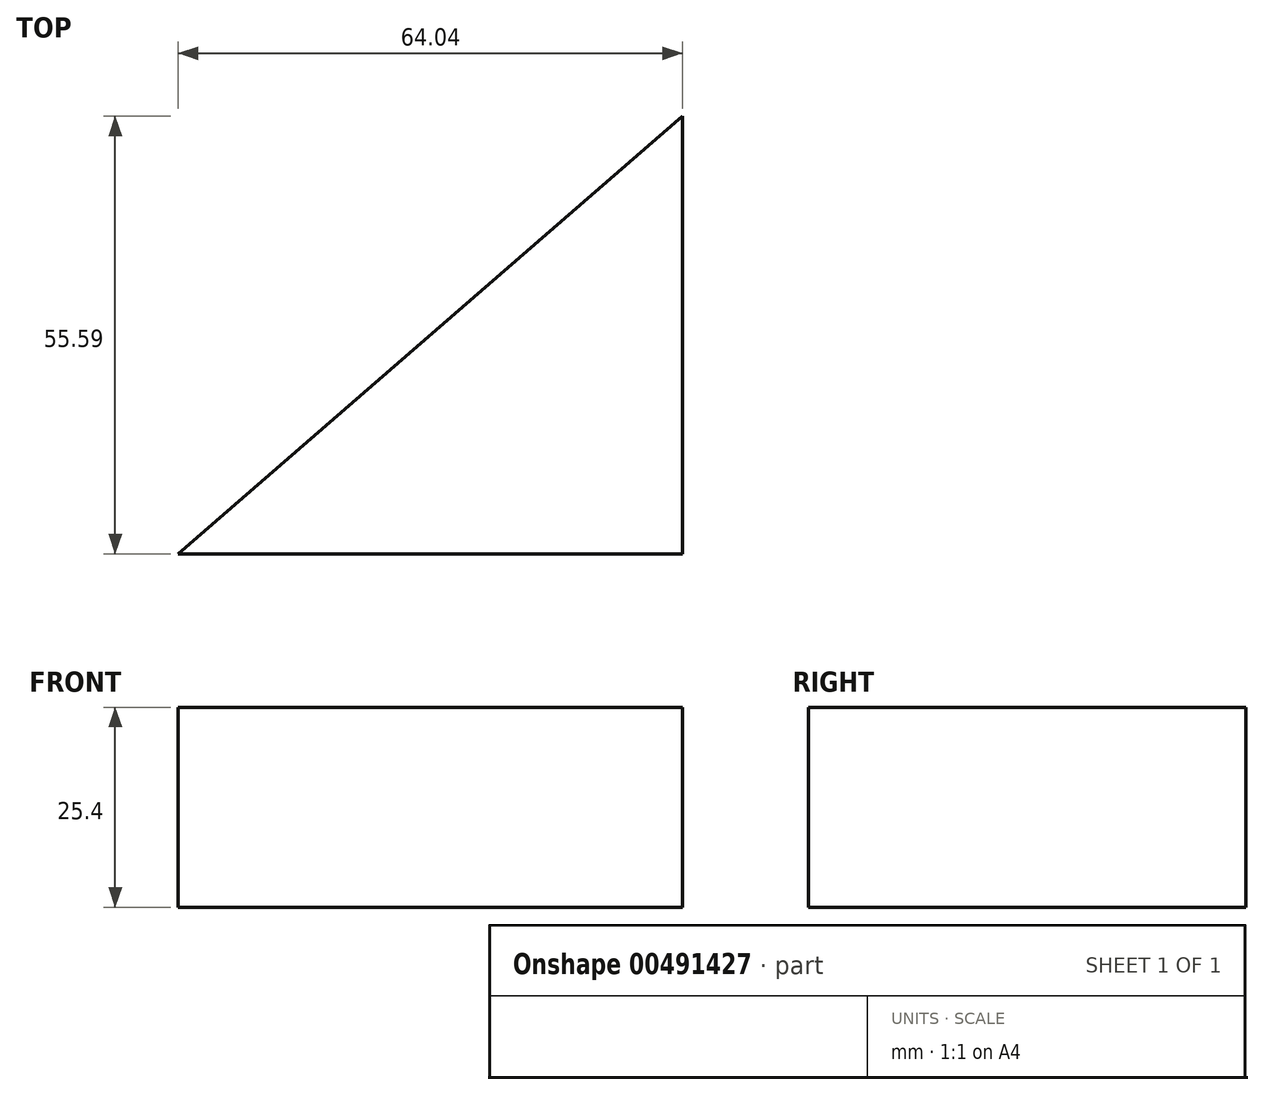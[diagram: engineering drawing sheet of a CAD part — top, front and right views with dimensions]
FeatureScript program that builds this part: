
annotation { "Feature Type Name" : "Feature", "Feature Type Description" : "" }
export const myFeature = defineFeature(function(context is Context, id is Id, definition is map)
    precondition{}
    {
        {
            var Q0;
            Q0=qCreatedBy(makeId("Top.planeOp"),FACE);
            var sketch = newSketch(context, id + "F0", { "sketchPlane" : qUnion([Q0])});
            skLineSegment(sketch, "E0", {"start": v(0, 0) * mm, "end": v(64.04, 55.6) * mm});
            skLineSegment(sketch, "E1", {"start": v(64.04, 55.6) * mm, "end": v(64.04, 0) * mm});
            skLineSegment(sketch, "E2", {"start": v(64.04, 0) * mm, "end": v(0, 0) * mm});
            skSolve(sketch);
        }
        {
            var Q0;
            Q0=makeQuery(id+"F0.imprint","IMPRINT",FACE,{"disambiguationData":[TD([[makeQuery(id+"F0.imprint","IMPRINT",EDGE,{"derivedFrom":sQuery(id+"F0.wireOp",EDGE,"E0")}),-1.0]])]});
            extrude(context, id + "F1", {"entities" : qUnion([Q0]), "depth" : 25.4 * mm});
        }
    });
